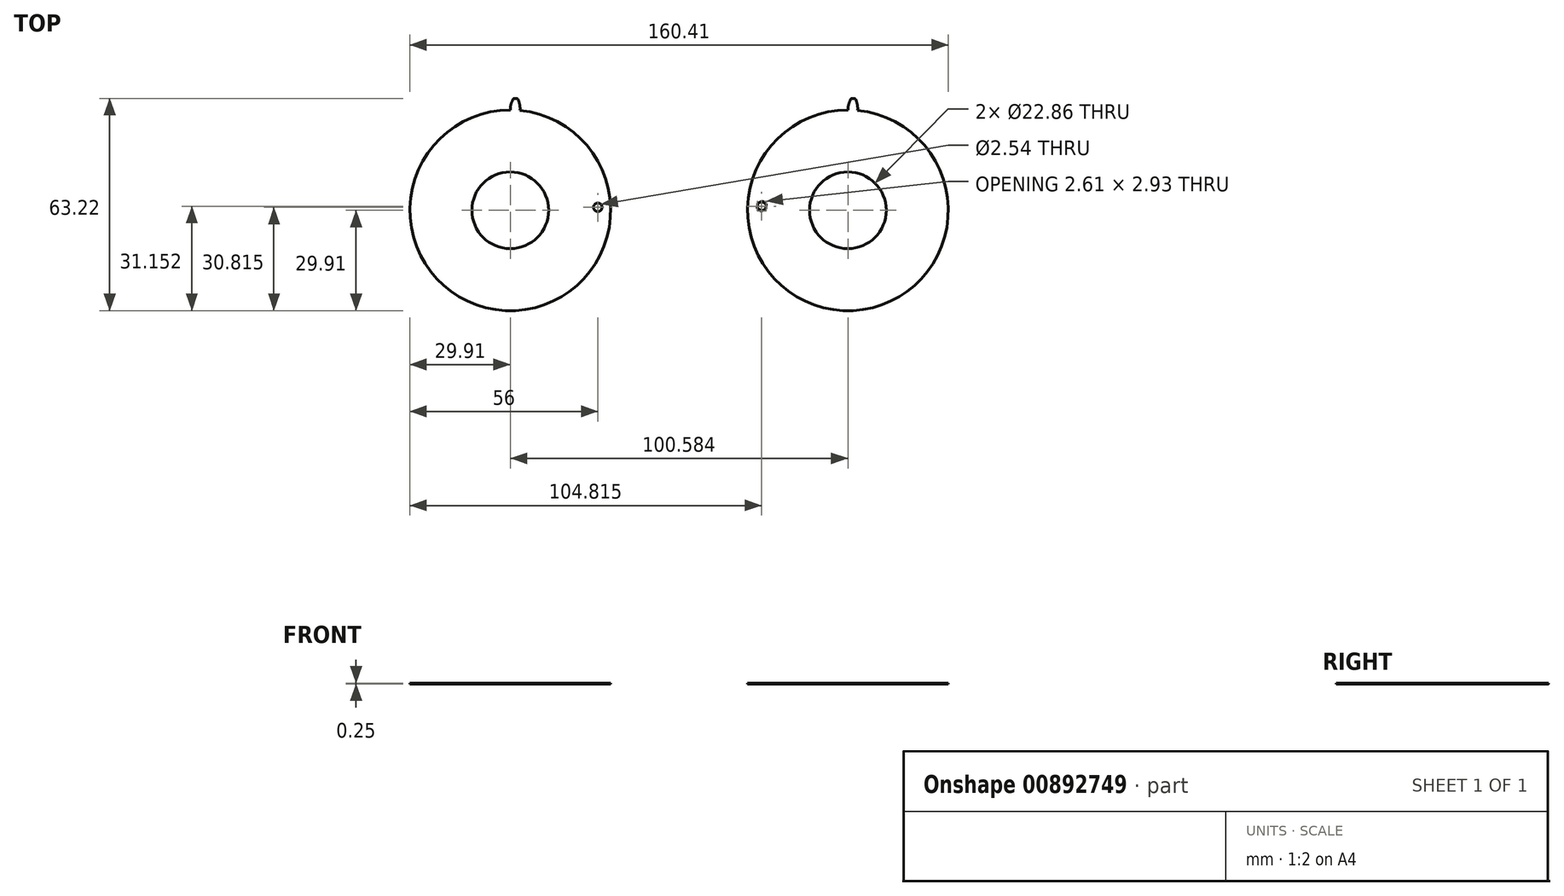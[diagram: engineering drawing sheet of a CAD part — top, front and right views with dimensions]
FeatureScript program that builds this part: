
annotation { "Feature Type Name" : "Feature", "Feature Type Description" : "" }
export const myFeature = defineFeature(function(context is Context, id is Id, definition is map)
    precondition{}
    {
        {
            assignVariable(context, id + "F0", {"name" : "N", "anyValue" : 16 * 2.5});
        }
        {
            assignVariable(context, id + "F1", {"name" : "Swid", "anyValue" : 0.25});
        }
        {
            var Q0;
            Q0=qCreatedBy(makeId("Top.planeOp"),FACE);
            var sketch = newSketch(context, id + "F2", { "sketchPlane" : qUnion([Q0])});
            skCircle(sketch, "E0", {"center": v(0, 0) * mm, "radius": 30.36 * mm, "construction": true});
            skCircle(sketch, "E1", {"center": v(0, 0) * mm, "radius": 31.75 * mm, "construction": true});
            skCircle(sketch, "E2", {"center": v(0, 0) * mm, "radius": 33.34 * mm});
            skLineSegment(sketch, "E3", {"start": v(0, 0) * mm, "end": v(0, 30.36) * mm, "construction": true});
            skLineSegment(sketch, "E4", {"start": v(0, 0) * mm, "end": v(1.99, 30.3) * mm, "construction": true});
            skLineSegment(sketch, "E5", {"start": v(0, 0) * mm, "end": v(3.96, 30.1) * mm, "construction": true});
            skLineSegment(sketch, "E6", {"start": v(0, 0) * mm, "end": v(5.92, 29.78) * mm, "construction": true});
            skLineSegment(sketch, "E7", {"start": v(0, 0) * mm, "end": v(7.86, 29.33) * mm, "construction": true});
            skCircle(sketch, "E8", {"center": v(0, 0) * mm, "radius": 29.91 * mm});
            skLineSegment(sketch, "E9", {"start": v(1.99, 30.3) * mm, "end": v(0, 30.43) * mm, "construction": true});
            skLineSegment(sketch, "E10", {"start": v(3.96, 30.1) * mm, "end": v(0.02, 30.62) * mm, "construction": true});
            skLineSegment(sketch, "E11", {"start": v(5.92, 29.78) * mm, "end": v(0.08, 30.94) * mm, "construction": true});
            skLineSegment(sketch, "E12", {"start": v(7.86, 29.33) * mm, "end": v(0.18, 31.39) * mm, "construction": true});
            skLineSegment(sketch, "E13", {"start": v(0, 0) * mm, "end": v(9.76, 28.75) * mm, "construction": true});
            skLineSegment(sketch, "E14", {"start": v(9.76, 28.75) * mm, "end": v(0.35, 31.95) * mm, "construction": true});
            skLineSegment(sketch, "E15", {"start": v(0, 0) * mm, "end": v(11.62, 28.05) * mm, "construction": true});
            skLineSegment(sketch, "E16", {"start": v(0, 0) * mm, "end": v(13.43, 27.23) * mm, "construction": true});
            skLineSegment(sketch, "E17", {"start": v(0, 0) * mm, "end": v(15.18, 26.3) * mm, "construction": true});
            skLineSegment(sketch, "E18", {"start": v(11.62, 28.05) * mm, "end": v(0.6, 32.61) * mm, "construction": true});
            skLineSegment(sketch, "E19", {"start": v(13.43, 27.23) * mm, "end": v(0.95, 33.38) * mm, "construction": true});
            skLineSegment(sketch, "E20", {"start": v(15.18, 26.3) * mm, "end": v(1.41, 34.24) * mm, "construction": true});
            skLineSegment(sketch, "E21", {"start": v(0, 0) * mm, "end": v(16.87, 25.25) * mm, "construction": true});
            skLineSegment(sketch, "E22", {"start": v(0, 0) * mm, "end": v(18.48, 24.09) * mm, "construction": true});
            skLineSegment(sketch, "E23", {"start": v(0, 0) * mm, "end": v(20.02, 22.83) * mm, "construction": true});
            skLineSegment(sketch, "E24", {"start": v(0, 0) * mm, "end": v(21.47, 21.47) * mm, "construction": true});
            skLineSegment(sketch, "E25", {"start": v(0, 0) * mm, "end": v(22.83, 20.02) * mm, "construction": true});
            skLineSegment(sketch, "E26", {"start": v(16.87, 25.25) * mm, "end": v(2, 35.18) * mm, "construction": true});
            skLineSegment(sketch, "E27", {"start": v(18.48, 24.09) * mm, "end": v(2.72, 36.19) * mm, "construction": true});
            skLineSegment(sketch, "E28", {"start": v(20.02, 22.83) * mm, "end": v(3.58, 37.24) * mm, "construction": true});
            skLineSegment(sketch, "E29", {"start": v(21.47, 21.47) * mm, "end": v(4.6, 38.33) * mm, "construction": true});
            skLineSegment(sketch, "E30", {"start": v(22.83, 20.02) * mm, "end": v(5.8, 39.44) * mm, "construction": true});
            skLineSegment(sketch, "E31", {"start": v(0, 0) * mm, "end": v(24.09, 18.48) * mm, "construction": true});
            skLineSegment(sketch, "E32", {"start": v(24.09, 18.48) * mm, "end": v(7.15, 40.56) * mm, "construction": true});
            skLineSegment(sketch, "E33", {"start": v(0, 0) * mm, "end": v(25.25, 16.87) * mm, "construction": true});
            skLineSegment(sketch, "E34", {"start": v(25.25, 16.87) * mm, "end": v(8.68, 41.65) * mm, "construction": true});
            skSolve(sketch);
        }
        {
            var Q0;
            Q0=qCreatedBy(makeId("Top.planeOp"),FACE);
            var sketch = newSketch(context, id + "F3", { "sketchPlane" : qUnion([Q0])});
            skLineSegment(sketch, "E35.0", {"start": v(24.09, 18.48) * mm, "end": v(7.15, 40.56) * mm, "construction": true});
            skLineSegment(sketch, "E35.1", {"start": v(22.83, 20.02) * mm, "end": v(5.8, 39.44) * mm, "construction": true});
            skLineSegment(sketch, "E35.2", {"start": v(21.47, 21.47) * mm, "end": v(4.6, 38.33) * mm, "construction": true});
            skLineSegment(sketch, "E35.3", {"start": v(20.02, 22.83) * mm, "end": v(3.58, 37.24) * mm, "construction": true});
            skLineSegment(sketch, "E35.4", {"start": v(18.48, 24.09) * mm, "end": v(2.72, 36.19) * mm, "construction": true});
            skLineSegment(sketch, "E35.5", {"start": v(16.87, 25.25) * mm, "end": v(2, 35.18) * mm, "construction": true});
            skLineSegment(sketch, "E35.6", {"start": v(15.18, 26.3) * mm, "end": v(1.41, 34.24) * mm, "construction": true});
            skLineSegment(sketch, "E35.7", {"start": v(13.43, 27.23) * mm, "end": v(0.95, 33.38) * mm, "construction": true});
            skLineSegment(sketch, "E35.8", {"start": v(11.62, 28.05) * mm, "end": v(0.6, 32.61) * mm, "construction": true});
            skLineSegment(sketch, "E35.9", {"start": v(9.76, 28.75) * mm, "end": v(0.35, 31.95) * mm, "construction": true});
            skLineSegment(sketch, "E35.10", {"start": v(7.86, 29.33) * mm, "end": v(0.18, 31.39) * mm, "construction": true});
            skLineSegment(sketch, "E35.11", {"start": v(5.92, 29.78) * mm, "end": v(0.08, 30.94) * mm, "construction": true});
            skLineSegment(sketch, "E35.12", {"start": v(3.96, 30.1) * mm, "end": v(0.02, 30.62) * mm, "construction": true});
            skLineSegment(sketch, "E35.13", {"start": v(1.99, 30.3) * mm, "end": v(0, 30.43) * mm, "construction": true});
            skCircle(sketch, "E35.14", {"center": v(0, 0) * mm, "radius": 30.36 * mm});
            skCircle(sketch, "E35.15", {"center": v(0, 0) * mm, "radius": 29.91 * mm});
            skCircle(sketch, "E35.16", {"center": v(0, 0) * mm, "radius": 31.75 * mm, "construction": true});
            skCircle(sketch, "E35.17", {"center": v(0, 0) * mm, "radius": 33.34 * mm});
            skLineSegment(sketch, "E36.0", {"start": v(25.25, 16.87) * mm, "end": v(8.68, 41.65) * mm, "construction": true});
            skLineSegment(sketch, "E37.0", {"start": v(0, 0) * mm, "end": v(0, 30.36) * mm, "construction": true});
            skFitSpline(sketch, "E38", {"points": [v(0, 30.36) * mm, v(0, 30.43) * mm, v(0.02, 30.62) * mm, v(0.08, 30.94) * mm, v(0.18, 31.39) * mm, v(0.35, 31.95) * mm, v(0.6, 32.61) * mm, v(0.95, 33.38) * mm, v(1.41, 34.24) * mm, v(2, 35.18) * mm, v(2.72, 36.19) * mm, v(3.58, 37.24) * mm, v(4.6, 38.33) * mm, v(5.8, 39.44) * mm, v(7.15, 40.56) * mm, v(8.68, 41.65) * mm, v(0, 0) * mm], "startDerivative": vector(0.68, 15.67) * mm, "endDerivative": vector(-81.92, -392.9) * mm});
            skLineSegment(sketch, "E39", {"start": v(0.29, 31.75) * mm, "end": v(0, 0) * mm, "construction": true});
            skLineSegment(sketch, "E40", {"start": v(0, 0) * mm, "end": v(1.6, 33.3) * mm, "construction": true});
            skFitSpline(sketch, "E41.MirrorCS", {"points": [v(2.93, 30.22) * mm, v(2.93, 30.29) * mm, v(2.93, 30.48) * mm, v(2.9, 30.8) * mm, v(2.85, 31.26) * mm, v(2.73, 31.83) * mm, v(2.54, 32.52) * mm, v(2.27, 33.32) * mm, v(1.9, 34.22) * mm, v(1.4, 35.21) * mm, v(0.78, 36.28) * mm, v(0.02, 37.41) * mm, v(-0.89, 38.6) * mm, v(-1.96, 39.82) * mm, v(-3.2, 41.06) * mm, v(-4.63, 42.3) * mm, v(0, 0) * mm], "startDerivative": vector(0.83, 15.67) * mm, "endDerivative": vector(43.65, -398.97) * mm});
            skLineSegment(sketch, "E42", {"start": v(2.93, 30.22) * mm, "end": v(2.88, 29.77) * mm});
            skLineSegment(sketch, "E43", {"start": v(0, 30.36) * mm, "end": v(0, 29.91) * mm});
            skSolve(sketch);
        }
        {
            var Q0;
            {var subQ3=sQuery(id+"F3.wireOp",EDGE,"E41.MirrorCS");var subQ6=sQuery(id+"F3.wireOp",EDGE,"E35.17");var subQ8=makeQuery(id+"F3.imprint","INTERSECT",VERTEX,{"disambiguationData":[OD(1.0)],"derivedFrom":[subQ6,subQ3]});Q0=makeQuery(id+"F3.imprint","IMPRINT",FACE,{"disambiguationData":[TD([[makeQuery(id+"F3.imprint","IMPRINT",EDGE,{"disambiguationData":[TD([[subQ8,-1.0]])],"derivedFrom":subQ6}),1.0]])]});}
            var Q1;
            {var subQ3=sQuery(id+"F3.wireOp",EDGE,"E41.MirrorCS");var subQ5=sQuery(id+"F3.wireOp",EDGE,"E35.15");var subQ6=makeQuery(id+"F3.imprint","INTERSECT",VERTEX,{"derivedFrom":[subQ5,subQ3]});Q1=makeQuery(id+"F3.imprint","IMPRINT",FACE,{"disambiguationData":[TD([[makeQuery(id+"F3.imprint","IMPRINT",EDGE,{"disambiguationData":[TD([[subQ6,-1.0]])],"derivedFrom":subQ5}),1.0]])]});}
            var Q2;
            {var subQ2=sQuery(id+"F3.wireOp",EDGE,"E42");Q2=makeQuery(id+"F3.imprint","IMPRINT",FACE,{"disambiguationData":[TD([[makeQuery(id+"F3.imprint","IMPRINT",EDGE,{"derivedFrom":subQ2}),-1.0]])]});}
            extrude(context, id + "F4", {"entities" : qUnion([Q0, Q1, Q2]), "depth" : (getVariable(context, 'Swid')) * mm, "offsetDistance" : 25.4 * mm});
        }
        {
            var Q0;
            Q0=qCreatedBy(makeId("Right.planeOp"),FACE);
            var sketch = newSketch(context, id + "F5", { "sketchPlane" : qUnion([Q0])});
            skLineSegment(sketch, "E44", {"start": v(0, 0) * mm, "end": v(0, 43.3) * mm, "construction": true});
            skSolve(sketch);
        }
        {
            var Q0;
            Q0=makeQuery(id+"F4.opExtrude","SWEPT_EDGE",EDGE,{"disambiguationData":[OSD([sQuery(id+"F3.wireOp",EDGE,"E35.17"),sQuery(id+"F3.wireOp",EDGE,"E41.MirrorCS")])]});
            var Q1;
            Q1=makeQuery(id+"F4.opExtrude","SWEPT_EDGE",EDGE,{"disambiguationData":[OSD([sQuery(id+"F3.wireOp",EDGE,"E35.17"),sQuery(id+"F3.wireOp",EDGE,"E38")])]});
            fillet(context, id + "F6", {"entities" : qUnion([Q0, Q1]), "radius" : 0.5 * mm, "tangentPropagation" : true, "allowEdgeOverflow" : false});
        }
        {
            var Q0;
            Q0=makeQuery(id+"F4.opExtrude","SWEPT_BODY",BODY,{"disambiguationData":[OSD([sQuery(id+"F3.wireOp",EDGE,"E35.15"),sQuery(id+"F3.wireOp",EDGE,"E35.17"),sQuery(id+"F3.wireOp",EDGE,"E38"),sQuery(id+"F3.wireOp",EDGE,"E41.MirrorCS"),sQuery(id+"F3.wireOp",EDGE,"9305e2c8-a00a-4cbc-a3b2-8fc88bc1717c"),sQuery(id+"F3.wireOp",EDGE,"f762f43d-eaf9-45ff-b6cd-062fd530227c")])]});
            var Q1;
            Q1=sQuery(id+"F5.wireOp",EDGE,"E44");
            circularPattern(context, id + "F7", {"operationType" : NewBodyOperationType.ADD, "entities" : qUnion([Q0]), "axis" : qUnion([Q1]), "angle" : (360 / getVariable(context, 'N')) * degree, "instanceCount" : getVariable(context, 'N'), "oppositeDirection" : true});
        }
        {
            var Q0;
            Q0=makeQuery(id+"F4.opExtrude","SWEPT_BODY",BODY,{"disambiguationData":[OSD([sQuery(id+"F3.wireOp",EDGE,"E35.15"),sQuery(id+"F3.wireOp",EDGE,"E35.17"),sQuery(id+"F3.wireOp",EDGE,"E38"),sQuery(id+"F3.wireOp",EDGE,"E41.MirrorCS"),sQuery(id+"F3.wireOp",EDGE,"E42"),sQuery(id+"F3.wireOp",EDGE,"E43")])]});
            transform(context, id + "F8", {"entities" : qUnion([Q0]), "transformType" : TransformType.TRANSLATION_3D, "dx" : 100.58 * mm, "dy" : 0 * mm, "dz" : 0 * mm, "makeCopy" : true});
        }
        {
            var Q0;
            {var subQ0=makeQuery(id+"F4.opExtrude","CAP_FACE",FACE,{"disambiguationData":[OSD([sQuery(id+"F3.wireOp",EDGE,"E35.15"),sQuery(id+"F3.wireOp",EDGE,"E35.17"),sQuery(id+"F3.wireOp",EDGE,"E38"),sQuery(id+"F3.wireOp",EDGE,"E41.MirrorCS"),sQuery(id+"F3.wireOp",EDGE,"E42"),sQuery(id+"F3.wireOp",EDGE,"E43")])],"isStart":false});Q0=makeQuery(id+"F7.boolean.opBoolean","MERGE",FACE,{"derivedFrom":[subQ0,makeQuery(id+"F7.opPattern","COPY",FACE,{"derivedFrom":subQ0,"instanceName":"1"}),makeQuery(id+"F7.opPattern","COPY",FACE,{"derivedFrom":subQ0,"instanceName":"2"}),makeQuery(id+"F7.opPattern","COPY",FACE,{"derivedFrom":subQ0,"instanceName":"3"}),makeQuery(id+"F7.opPattern","COPY",FACE,{"derivedFrom":subQ0,"instanceName":"4"}),makeQuery(id+"F7.opPattern","COPY",FACE,{"derivedFrom":subQ0,"instanceName":"5"}),makeQuery(id+"F7.opPattern","COPY",FACE,{"derivedFrom":subQ0,"instanceName":"6"}),makeQuery(id+"F7.opPattern","COPY",FACE,{"derivedFrom":subQ0,"instanceName":"7"}),makeQuery(id+"F7.opPattern","COPY",FACE,{"derivedFrom":subQ0,"instanceName":"8"}),makeQuery(id+"F7.opPattern","COPY",FACE,{"derivedFrom":subQ0,"instanceName":"9"}),makeQuery(id+"F7.opPattern","COPY",FACE,{"derivedFrom":subQ0,"instanceName":"10"}),makeQuery(id+"F7.opPattern","COPY",FACE,{"derivedFrom":subQ0,"instanceName":"11"}),makeQuery(id+"F7.opPattern","COPY",FACE,{"derivedFrom":subQ0,"instanceName":"12"}),makeQuery(id+"F7.opPattern","COPY",FACE,{"derivedFrom":subQ0,"instanceName":"13"}),makeQuery(id+"F7.opPattern","COPY",FACE,{"derivedFrom":subQ0,"instanceName":"14"}),makeQuery(id+"F7.opPattern","COPY",FACE,{"derivedFrom":subQ0,"instanceName":"15"}),makeQuery(id+"F7.opPattern","COPY",FACE,{"derivedFrom":subQ0,"instanceName":"16"}),makeQuery(id+"F7.opPattern","COPY",FACE,{"derivedFrom":subQ0,"instanceName":"17"}),makeQuery(id+"F7.opPattern","COPY",FACE,{"derivedFrom":subQ0,"instanceName":"18"}),makeQuery(id+"F7.opPattern","COPY",FACE,{"derivedFrom":subQ0,"instanceName":"19"}),makeQuery(id+"F7.opPattern","COPY",FACE,{"derivedFrom":subQ0,"instanceName":"20"}),makeQuery(id+"F7.opPattern","COPY",FACE,{"derivedFrom":subQ0,"instanceName":"21"}),makeQuery(id+"F7.opPattern","COPY",FACE,{"derivedFrom":subQ0,"instanceName":"22"}),makeQuery(id+"F7.opPattern","COPY",FACE,{"derivedFrom":subQ0,"instanceName":"23"}),makeQuery(id+"F7.opPattern","COPY",FACE,{"derivedFrom":subQ0,"instanceName":"24"}),makeQuery(id+"F7.opPattern","COPY",FACE,{"derivedFrom":subQ0,"instanceName":"25"}),makeQuery(id+"F7.opPattern","COPY",FACE,{"derivedFrom":subQ0,"instanceName":"26"}),makeQuery(id+"F7.opPattern","COPY",FACE,{"derivedFrom":subQ0,"instanceName":"27"}),makeQuery(id+"F7.opPattern","COPY",FACE,{"derivedFrom":subQ0,"instanceName":"28"}),makeQuery(id+"F7.opPattern","COPY",FACE,{"derivedFrom":subQ0,"instanceName":"29"}),makeQuery(id+"F7.opPattern","COPY",FACE,{"derivedFrom":subQ0,"instanceName":"30"}),makeQuery(id+"F7.opPattern","COPY",FACE,{"derivedFrom":subQ0,"instanceName":"31"}),makeQuery(id+"F7.opPattern","COPY",FACE,{"derivedFrom":subQ0,"instanceName":"32"}),makeQuery(id+"F7.opPattern","COPY",FACE,{"derivedFrom":subQ0,"instanceName":"33"}),makeQuery(id+"F7.opPattern","COPY",FACE,{"derivedFrom":subQ0,"instanceName":"34"}),makeQuery(id+"F7.opPattern","COPY",FACE,{"derivedFrom":subQ0,"instanceName":"35"}),makeQuery(id+"F7.opPattern","COPY",FACE,{"derivedFrom":subQ0,"instanceName":"36"}),makeQuery(id+"F7.opPattern","COPY",FACE,{"derivedFrom":subQ0,"instanceName":"37"}),makeQuery(id+"F7.opPattern","COPY",FACE,{"derivedFrom":subQ0,"instanceName":"38"}),makeQuery(id+"F7.opPattern","COPY",FACE,{"derivedFrom":subQ0,"instanceName":"39"})]});}
            var sketch = newSketch(context, id + "F9", { "sketchPlane" : qUnion([Q0])});
            skCircle(sketch, "E45", {"center": v(0, 0) * mm, "radius": 4.1 * mm});
            skLineSegment(sketch, "E46", {"start": v(29.9, 0.9) * mm, "end": v(0, 0) * mm, "construction": true});
            skLineSegment(sketch, "E47", {"start": v(2.62, -3.15) * mm, "end": v(2.43, 3.3) * mm});
            skSolve(sketch);
        }
        {
            var Q0;
            {var subQ0=sQuery(id+"F9.wireOp",EDGE,"E47");Q0=makeQuery(id+"F9.imprint","IMPRINT",FACE,{"disambiguationData":[TD([[makeQuery(id+"F9.imprint","IMPRINT",EDGE,{"derivedFrom":subQ0}),1.0]])]});}
            extrude(context, id + "F10", {"entities" : qUnion([Q0]), "operationType" : NewBodyOperationType.REMOVE, "endBound" : BoundingType.THROUGH_ALL, "oppositeDirection" : true, "depth" : 25.4 * mm, "offsetDistance" : 25.4 * mm});
        }
        {
            var Q0;
            {var subQ0=makeQuery(id+"F4.opExtrude","CAP_FACE",FACE,{"disambiguationData":[OSD([sQuery(id+"F3.wireOp",EDGE,"E35.15"),sQuery(id+"F3.wireOp",EDGE,"E35.17"),sQuery(id+"F3.wireOp",EDGE,"E38"),sQuery(id+"F3.wireOp",EDGE,"E41.MirrorCS"),sQuery(id+"F3.wireOp",EDGE,"E42"),sQuery(id+"F3.wireOp",EDGE,"E43")])],"isStart":false});Q0=makeQuery(id+"F7.boolean.opBoolean","MERGE",FACE,{"derivedFrom":[subQ0,makeQuery(id+"F7.opPattern","COPY",FACE,{"derivedFrom":subQ0,"instanceName":"1"}),makeQuery(id+"F7.opPattern","COPY",FACE,{"derivedFrom":subQ0,"instanceName":"2"}),makeQuery(id+"F7.opPattern","COPY",FACE,{"derivedFrom":subQ0,"instanceName":"3"}),makeQuery(id+"F7.opPattern","COPY",FACE,{"derivedFrom":subQ0,"instanceName":"4"}),makeQuery(id+"F7.opPattern","COPY",FACE,{"derivedFrom":subQ0,"instanceName":"5"}),makeQuery(id+"F7.opPattern","COPY",FACE,{"derivedFrom":subQ0,"instanceName":"6"}),makeQuery(id+"F7.opPattern","COPY",FACE,{"derivedFrom":subQ0,"instanceName":"7"}),makeQuery(id+"F7.opPattern","COPY",FACE,{"derivedFrom":subQ0,"instanceName":"8"}),makeQuery(id+"F7.opPattern","COPY",FACE,{"derivedFrom":subQ0,"instanceName":"9"}),makeQuery(id+"F7.opPattern","COPY",FACE,{"derivedFrom":subQ0,"instanceName":"10"}),makeQuery(id+"F7.opPattern","COPY",FACE,{"derivedFrom":subQ0,"instanceName":"11"}),makeQuery(id+"F7.opPattern","COPY",FACE,{"derivedFrom":subQ0,"instanceName":"12"}),makeQuery(id+"F7.opPattern","COPY",FACE,{"derivedFrom":subQ0,"instanceName":"13"}),makeQuery(id+"F7.opPattern","COPY",FACE,{"derivedFrom":subQ0,"instanceName":"14"}),makeQuery(id+"F7.opPattern","COPY",FACE,{"derivedFrom":subQ0,"instanceName":"15"}),makeQuery(id+"F7.opPattern","COPY",FACE,{"derivedFrom":subQ0,"instanceName":"16"}),makeQuery(id+"F7.opPattern","COPY",FACE,{"derivedFrom":subQ0,"instanceName":"17"}),makeQuery(id+"F7.opPattern","COPY",FACE,{"derivedFrom":subQ0,"instanceName":"18"}),makeQuery(id+"F7.opPattern","COPY",FACE,{"derivedFrom":subQ0,"instanceName":"19"}),makeQuery(id+"F7.opPattern","COPY",FACE,{"derivedFrom":subQ0,"instanceName":"20"}),makeQuery(id+"F7.opPattern","COPY",FACE,{"derivedFrom":subQ0,"instanceName":"21"}),makeQuery(id+"F7.opPattern","COPY",FACE,{"derivedFrom":subQ0,"instanceName":"22"}),makeQuery(id+"F7.opPattern","COPY",FACE,{"derivedFrom":subQ0,"instanceName":"23"}),makeQuery(id+"F7.opPattern","COPY",FACE,{"derivedFrom":subQ0,"instanceName":"24"}),makeQuery(id+"F7.opPattern","COPY",FACE,{"derivedFrom":subQ0,"instanceName":"25"}),makeQuery(id+"F7.opPattern","COPY",FACE,{"derivedFrom":subQ0,"instanceName":"26"}),makeQuery(id+"F7.opPattern","COPY",FACE,{"derivedFrom":subQ0,"instanceName":"27"}),makeQuery(id+"F7.opPattern","COPY",FACE,{"derivedFrom":subQ0,"instanceName":"28"}),makeQuery(id+"F7.opPattern","COPY",FACE,{"derivedFrom":subQ0,"instanceName":"29"}),makeQuery(id+"F7.opPattern","COPY",FACE,{"derivedFrom":subQ0,"instanceName":"30"}),makeQuery(id+"F7.opPattern","COPY",FACE,{"derivedFrom":subQ0,"instanceName":"31"}),makeQuery(id+"F7.opPattern","COPY",FACE,{"derivedFrom":subQ0,"instanceName":"32"}),makeQuery(id+"F7.opPattern","COPY",FACE,{"derivedFrom":subQ0,"instanceName":"33"}),makeQuery(id+"F7.opPattern","COPY",FACE,{"derivedFrom":subQ0,"instanceName":"34"}),makeQuery(id+"F7.opPattern","COPY",FACE,{"derivedFrom":subQ0,"instanceName":"35"}),makeQuery(id+"F7.opPattern","COPY",FACE,{"derivedFrom":subQ0,"instanceName":"36"}),makeQuery(id+"F7.opPattern","COPY",FACE,{"derivedFrom":subQ0,"instanceName":"37"}),makeQuery(id+"F7.opPattern","COPY",FACE,{"derivedFrom":subQ0,"instanceName":"38"}),makeQuery(id+"F7.opPattern","COPY",FACE,{"derivedFrom":subQ0,"instanceName":"39"})]});}
            var sketch = newSketch(context, id + "F11", { "sketchPlane" : qUnion([Q0])});
            skCircle(sketch, "E48", {"center": v(0, 0) * mm, "radius": 11.43 * mm});
            skCircle(sketch, "E49", {"center": v(26.09, 0.9) * mm, "radius": 1.27 * mm});
            skPoint(sketch, "E49.centerSnap0", {"position": v(29.9, 0.9) * mm});
            skSolve(sketch);
        }
        {
            var Q0;
            Q0=makeQuery(id+"F11.imprint","IMPRINT",FACE,{"disambiguationData":[TD([[makeQuery(id+"F11.imprint","IMPRINT",EDGE,{"derivedFrom":sQuery(id+"F11.wireOp",EDGE,"E48")}),1.0]])]});
            var Q1;
            Q1=makeQuery(id+"F11.imprint","IMPRINT",FACE,{"disambiguationData":[TD([[makeQuery(id+"F11.imprint","IMPRINT",EDGE,{"derivedFrom":sQuery(id+"F11.wireOp",EDGE,"ih8nmMkE-TSqh-M1XZ-P10M-uwXWHLw3eGEC")}),1.0]])]});
            var Q2;
            Q2=makeQuery(id+"F11.imprint","IMPRINT",FACE,{"disambiguationData":[TD([[makeQuery(id+"F11.imprint","IMPRINT",EDGE,{"derivedFrom":sQuery(id+"F11.wireOp",EDGE,"E49")}),1.0]])]});
            extrude(context, id + "F12", {"entities" : qUnion([Q0, Q1, Q2]), "operationType" : NewBodyOperationType.REMOVE, "oppositeDirection" : true, "depth" : 0.25 * mm, "offsetDistance" : 25.4 * mm});
        }
        {
            var Q0;
            {var subQ0=makeQuery(id+"F4.opExtrude","CAP_FACE",FACE,{"disambiguationData":[OSD([sQuery(id+"F3.wireOp",EDGE,"E35.15"),sQuery(id+"F3.wireOp",EDGE,"E35.17"),sQuery(id+"F3.wireOp",EDGE,"E38"),sQuery(id+"F3.wireOp",EDGE,"E41.MirrorCS"),sQuery(id+"F3.wireOp",EDGE,"E42"),sQuery(id+"F3.wireOp",EDGE,"E43")])],"isStart":false});Q0=makeQuery(id+"F8.opPattern","COPY",FACE,{"derivedFrom":makeQuery(id+"F7.boolean.opBoolean","MERGE",FACE,{"derivedFrom":[subQ0,makeQuery(id+"F7.opPattern","COPY",FACE,{"derivedFrom":subQ0,"instanceName":"1"}),makeQuery(id+"F7.opPattern","COPY",FACE,{"derivedFrom":subQ0,"instanceName":"2"}),makeQuery(id+"F7.opPattern","COPY",FACE,{"derivedFrom":subQ0,"instanceName":"3"}),makeQuery(id+"F7.opPattern","COPY",FACE,{"derivedFrom":subQ0,"instanceName":"4"}),makeQuery(id+"F7.opPattern","COPY",FACE,{"derivedFrom":subQ0,"instanceName":"5"}),makeQuery(id+"F7.opPattern","COPY",FACE,{"derivedFrom":subQ0,"instanceName":"6"}),makeQuery(id+"F7.opPattern","COPY",FACE,{"derivedFrom":subQ0,"instanceName":"7"}),makeQuery(id+"F7.opPattern","COPY",FACE,{"derivedFrom":subQ0,"instanceName":"8"}),makeQuery(id+"F7.opPattern","COPY",FACE,{"derivedFrom":subQ0,"instanceName":"9"}),makeQuery(id+"F7.opPattern","COPY",FACE,{"derivedFrom":subQ0,"instanceName":"10"}),makeQuery(id+"F7.opPattern","COPY",FACE,{"derivedFrom":subQ0,"instanceName":"11"}),makeQuery(id+"F7.opPattern","COPY",FACE,{"derivedFrom":subQ0,"instanceName":"12"}),makeQuery(id+"F7.opPattern","COPY",FACE,{"derivedFrom":subQ0,"instanceName":"13"}),makeQuery(id+"F7.opPattern","COPY",FACE,{"derivedFrom":subQ0,"instanceName":"14"}),makeQuery(id+"F7.opPattern","COPY",FACE,{"derivedFrom":subQ0,"instanceName":"15"}),makeQuery(id+"F7.opPattern","COPY",FACE,{"derivedFrom":subQ0,"instanceName":"16"}),makeQuery(id+"F7.opPattern","COPY",FACE,{"derivedFrom":subQ0,"instanceName":"17"}),makeQuery(id+"F7.opPattern","COPY",FACE,{"derivedFrom":subQ0,"instanceName":"18"}),makeQuery(id+"F7.opPattern","COPY",FACE,{"derivedFrom":subQ0,"instanceName":"19"}),makeQuery(id+"F7.opPattern","COPY",FACE,{"derivedFrom":subQ0,"instanceName":"20"}),makeQuery(id+"F7.opPattern","COPY",FACE,{"derivedFrom":subQ0,"instanceName":"21"}),makeQuery(id+"F7.opPattern","COPY",FACE,{"derivedFrom":subQ0,"instanceName":"22"}),makeQuery(id+"F7.opPattern","COPY",FACE,{"derivedFrom":subQ0,"instanceName":"23"}),makeQuery(id+"F7.opPattern","COPY",FACE,{"derivedFrom":subQ0,"instanceName":"24"}),makeQuery(id+"F7.opPattern","COPY",FACE,{"derivedFrom":subQ0,"instanceName":"25"}),makeQuery(id+"F7.opPattern","COPY",FACE,{"derivedFrom":subQ0,"instanceName":"26"}),makeQuery(id+"F7.opPattern","COPY",FACE,{"derivedFrom":subQ0,"instanceName":"27"}),makeQuery(id+"F7.opPattern","COPY",FACE,{"derivedFrom":subQ0,"instanceName":"28"}),makeQuery(id+"F7.opPattern","COPY",FACE,{"derivedFrom":subQ0,"instanceName":"29"}),makeQuery(id+"F7.opPattern","COPY",FACE,{"derivedFrom":subQ0,"instanceName":"30"}),makeQuery(id+"F7.opPattern","COPY",FACE,{"derivedFrom":subQ0,"instanceName":"31"}),makeQuery(id+"F7.opPattern","COPY",FACE,{"derivedFrom":subQ0,"instanceName":"32"}),makeQuery(id+"F7.opPattern","COPY",FACE,{"derivedFrom":subQ0,"instanceName":"33"}),makeQuery(id+"F7.opPattern","COPY",FACE,{"derivedFrom":subQ0,"instanceName":"34"}),makeQuery(id+"F7.opPattern","COPY",FACE,{"derivedFrom":subQ0,"instanceName":"35"}),makeQuery(id+"F7.opPattern","COPY",FACE,{"derivedFrom":subQ0,"instanceName":"36"}),makeQuery(id+"F7.opPattern","COPY",FACE,{"derivedFrom":subQ0,"instanceName":"37"}),makeQuery(id+"F7.opPattern","COPY",FACE,{"derivedFrom":subQ0,"instanceName":"38"}),makeQuery(id+"F7.opPattern","COPY",FACE,{"derivedFrom":subQ0,"instanceName":"39"})]}),"instanceName":"1"});}
            var sketch = newSketch(context, id + "F13", { "sketchPlane" : qUnion([Q0])});
            skCircle(sketch, "E50", {"center": v(100.58, 0) * mm, "radius": 4.1 * mm});
            skLineSegment(sketch, "E51", {"start": v(98.22, 3.35) * mm, "end": v(97.9, -3.1) * mm});
            skLineSegment(sketch, "E52", {"start": v(67.3, 1.6) * mm, "end": v(98.06, 0.12) * mm, "construction": true});
            skPoint(sketch, "E52.startSnap0", {"position": v(67.29, 1.6) * mm});
            skCircle(sketch, "E53.cCircle", {"center": v(74.9, 1.24) * mm, "radius": 1.27 * mm, "construction": true});
            skLineSegment(sketch, "E53.0", {"start": v(73.6, 0.57) * mm, "end": v(73.67, 2.04) * mm});
            skLineSegment(sketch, "E53.1", {"start": v(73.67, 2.04) * mm, "end": v(74.98, 2.7) * mm});
            skLineSegment(sketch, "E53.2", {"start": v(74.98, 2.7) * mm, "end": v(76.2, 1.91) * mm});
            skLineSegment(sketch, "E53.3", {"start": v(76.2, 1.91) * mm, "end": v(76.14, 0.45) * mm});
            skLineSegment(sketch, "E53.4", {"start": v(76.14, 0.45) * mm, "end": v(74.83, -0.22) * mm});
            skLineSegment(sketch, "E53.5", {"start": v(74.83, -0.22) * mm, "end": v(73.6, 0.57) * mm});
            skPoint(sketch, "E53.0.midPoint", {"position": v(73.64, 1.3) * mm});
            skSolve(sketch);
        }
        {
            var Q0;
            {var subQ0=sQuery(id+"F13.wireOp",EDGE,"E51");Q0=makeQuery(id+"F13.imprint","IMPRINT",FACE,{"disambiguationData":[TD([[makeQuery(id+"F13.imprint","IMPRINT",EDGE,{"derivedFrom":subQ0}),1.0]])]});}
            extrude(context, id + "F14", {"entities" : qUnion([Q0]), "operationType" : NewBodyOperationType.REMOVE, "oppositeDirection" : true, "depth" : 25.4 * mm, "offsetDistance" : 25.4 * mm});
        }
        {
            var Q0;
            {var subQ0=makeQuery(id+"F4.opExtrude","CAP_FACE",FACE,{"disambiguationData":[OSD([sQuery(id+"F3.wireOp",EDGE,"E35.15"),sQuery(id+"F3.wireOp",EDGE,"E35.17"),sQuery(id+"F3.wireOp",EDGE,"E38"),sQuery(id+"F3.wireOp",EDGE,"E41.MirrorCS"),sQuery(id+"F3.wireOp",EDGE,"E42"),sQuery(id+"F3.wireOp",EDGE,"E43")])],"isStart":false});Q0=makeQuery(id+"F8.opPattern","COPY",FACE,{"derivedFrom":makeQuery(id+"F7.boolean.opBoolean","MERGE",FACE,{"derivedFrom":[subQ0,makeQuery(id+"F7.opPattern","COPY",FACE,{"derivedFrom":subQ0,"instanceName":"1"}),makeQuery(id+"F7.opPattern","COPY",FACE,{"derivedFrom":subQ0,"instanceName":"2"}),makeQuery(id+"F7.opPattern","COPY",FACE,{"derivedFrom":subQ0,"instanceName":"3"}),makeQuery(id+"F7.opPattern","COPY",FACE,{"derivedFrom":subQ0,"instanceName":"4"}),makeQuery(id+"F7.opPattern","COPY",FACE,{"derivedFrom":subQ0,"instanceName":"5"}),makeQuery(id+"F7.opPattern","COPY",FACE,{"derivedFrom":subQ0,"instanceName":"6"}),makeQuery(id+"F7.opPattern","COPY",FACE,{"derivedFrom":subQ0,"instanceName":"7"}),makeQuery(id+"F7.opPattern","COPY",FACE,{"derivedFrom":subQ0,"instanceName":"8"}),makeQuery(id+"F7.opPattern","COPY",FACE,{"derivedFrom":subQ0,"instanceName":"9"}),makeQuery(id+"F7.opPattern","COPY",FACE,{"derivedFrom":subQ0,"instanceName":"10"}),makeQuery(id+"F7.opPattern","COPY",FACE,{"derivedFrom":subQ0,"instanceName":"11"}),makeQuery(id+"F7.opPattern","COPY",FACE,{"derivedFrom":subQ0,"instanceName":"12"}),makeQuery(id+"F7.opPattern","COPY",FACE,{"derivedFrom":subQ0,"instanceName":"13"}),makeQuery(id+"F7.opPattern","COPY",FACE,{"derivedFrom":subQ0,"instanceName":"14"}),makeQuery(id+"F7.opPattern","COPY",FACE,{"derivedFrom":subQ0,"instanceName":"15"}),makeQuery(id+"F7.opPattern","COPY",FACE,{"derivedFrom":subQ0,"instanceName":"16"}),makeQuery(id+"F7.opPattern","COPY",FACE,{"derivedFrom":subQ0,"instanceName":"17"}),makeQuery(id+"F7.opPattern","COPY",FACE,{"derivedFrom":subQ0,"instanceName":"18"}),makeQuery(id+"F7.opPattern","COPY",FACE,{"derivedFrom":subQ0,"instanceName":"19"}),makeQuery(id+"F7.opPattern","COPY",FACE,{"derivedFrom":subQ0,"instanceName":"20"}),makeQuery(id+"F7.opPattern","COPY",FACE,{"derivedFrom":subQ0,"instanceName":"21"}),makeQuery(id+"F7.opPattern","COPY",FACE,{"derivedFrom":subQ0,"instanceName":"22"}),makeQuery(id+"F7.opPattern","COPY",FACE,{"derivedFrom":subQ0,"instanceName":"23"}),makeQuery(id+"F7.opPattern","COPY",FACE,{"derivedFrom":subQ0,"instanceName":"24"}),makeQuery(id+"F7.opPattern","COPY",FACE,{"derivedFrom":subQ0,"instanceName":"25"}),makeQuery(id+"F7.opPattern","COPY",FACE,{"derivedFrom":subQ0,"instanceName":"26"}),makeQuery(id+"F7.opPattern","COPY",FACE,{"derivedFrom":subQ0,"instanceName":"27"}),makeQuery(id+"F7.opPattern","COPY",FACE,{"derivedFrom":subQ0,"instanceName":"28"}),makeQuery(id+"F7.opPattern","COPY",FACE,{"derivedFrom":subQ0,"instanceName":"29"}),makeQuery(id+"F7.opPattern","COPY",FACE,{"derivedFrom":subQ0,"instanceName":"30"}),makeQuery(id+"F7.opPattern","COPY",FACE,{"derivedFrom":subQ0,"instanceName":"31"}),makeQuery(id+"F7.opPattern","COPY",FACE,{"derivedFrom":subQ0,"instanceName":"32"}),makeQuery(id+"F7.opPattern","COPY",FACE,{"derivedFrom":subQ0,"instanceName":"33"}),makeQuery(id+"F7.opPattern","COPY",FACE,{"derivedFrom":subQ0,"instanceName":"34"}),makeQuery(id+"F7.opPattern","COPY",FACE,{"derivedFrom":subQ0,"instanceName":"35"}),makeQuery(id+"F7.opPattern","COPY",FACE,{"derivedFrom":subQ0,"instanceName":"36"}),makeQuery(id+"F7.opPattern","COPY",FACE,{"derivedFrom":subQ0,"instanceName":"37"}),makeQuery(id+"F7.opPattern","COPY",FACE,{"derivedFrom":subQ0,"instanceName":"38"}),makeQuery(id+"F7.opPattern","COPY",FACE,{"derivedFrom":subQ0,"instanceName":"39"})]}),"instanceName":"1"});}
            var sketch = newSketch(context, id + "F15", { "sketchPlane" : qUnion([Q0])});
            skCircle(sketch, "E54", {"center": v(100.58, 0) * mm, "radius": 11.43 * mm});
            skLineSegment(sketch, "E55.0.0", {"start": v(73.6, 0.57) * mm, "end": v(74.83, -0.22) * mm});
            skLineSegment(sketch, "E55.0.1", {"start": v(74.83, -0.22) * mm, "end": v(76.14, 0.45) * mm});
            skLineSegment(sketch, "E55.0.2", {"start": v(76.14, 0.45) * mm, "end": v(76.2, 1.91) * mm});
            skLineSegment(sketch, "E55.0.3", {"start": v(76.2, 1.91) * mm, "end": v(74.98, 2.7) * mm});
            skLineSegment(sketch, "E55.0.4", {"start": v(74.98, 2.7) * mm, "end": v(73.67, 2.04) * mm});
            skLineSegment(sketch, "E55.0.5", {"start": v(73.67, 2.04) * mm, "end": v(73.6, 0.57) * mm});
            skSolve(sketch);
        }
        {
            var Q0;
            Q0=qSketchRegion(id+"F15",true);
            extrude(context, id + "F16", {"entities" : qUnion([Q0]), "operationType" : NewBodyOperationType.REMOVE, "oppositeDirection" : true, "depth" : 0.25 * mm, "offsetDistance" : 25.4 * mm});
        }
    });
